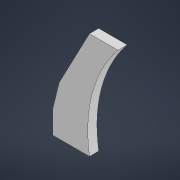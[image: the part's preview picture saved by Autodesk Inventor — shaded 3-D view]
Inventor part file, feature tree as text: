
AUTODESK INVENTOR PART (.ipt)
format: ipt  version: 2022 (Build 260153000, 153)  size: 98,304 bytes
history: native  units: in
note: dims shown in document units (in); Inventor stores cm internally (conversion verified against a paired STEP export)
features: extrude x1, chamfer x1, sketch x1
ambient origin geometry x8: Origin, YZ Plane, XZ Plane, XY Plane, X Axis, Y Axis, Z Axis, Center Point
bodies: Solid1 (feature_tree)
feature tree (3):
  extrude  "Extrusion1"  Depth=3.1496in
  chamfer  "Chamfer1"  Distance=0.7874in
  sketch  "Sketch1"  dims[d2=9.4488in d4=3.1496in d5=0.7874in d6=0.0in d7=1.1811in d8=0.0787in d9=45.0deg]
